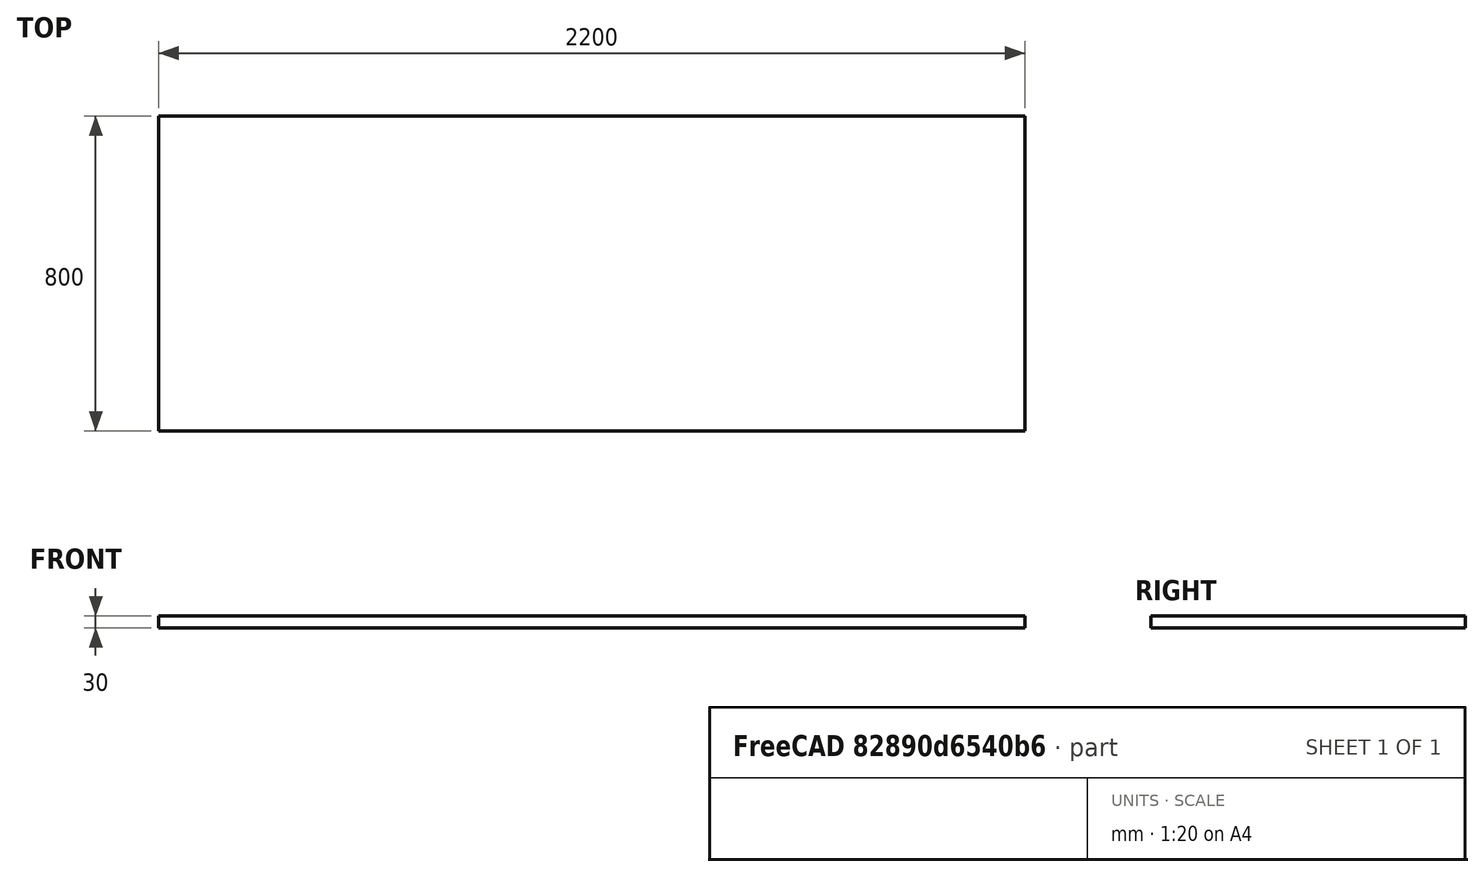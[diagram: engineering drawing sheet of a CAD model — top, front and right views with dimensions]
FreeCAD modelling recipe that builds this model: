
FCSTD DOCUMENT  (FreeCAD 1.0R39109 (Git))
Label: 021_top_sheet_30mm
License: All rights reserved
LicenseURL: http://en.wikipedia.org/wiki/All_rights_reserved
objects: Spreadsheet::Sheet×1, Sketcher::SketchObject×1, PartDesign::Pad×1, PartDesign::Body×1
note: 6 computed .brp shape members not serialized (recipe doc carries the construction recipe); baked Part::Feature solids carry a one-line shape summary decoded from their .brp

FEATURE [Spreadsheet::Sheet] Spreadsheet
  cells = A4='length; B4(length)=2200; A5='width; B5(width)=800; A6='height; B6(height)=30
FEATURE [Sketcher::SketchObject] Sketch
  ArcFitTolerance = 1e-06
  AttachmentSupport = -> [XY_Plane]
  FullyConstrained = true
  MakeInternals = false
  MapMode = 5
  expr: Constraints[11] = Spreadsheet.length
  expr: Constraints[12] = Spreadsheet.width
  sketch-geometry (5):
    g0: LineSegment StartX=-1100 StartY=400 StartZ=0 EndX=-1100 EndY=-400 EndZ=0
    g1: LineSegment StartX=-1100 StartY=-400 StartZ=0 EndX=1100 EndY=-400 EndZ=0
    g2: LineSegment StartX=1100 StartY=-400 StartZ=0 EndX=1100 EndY=400 EndZ=0
    g3: LineSegment StartX=1100 StartY=400 StartZ=0 EndX=-1100 EndY=400 EndZ=0
    g4: LineSegment [constr] StartX=-1100 StartY=400 StartZ=0 EndX=1100 EndY=-400 EndZ=0
  constraints (13):
    c: Coincident(g0,g1)
    c: Coincident(g1,g2)
    c: Coincident(g2,g3)
    c: Coincident(g3,g0)
    c: Vertical(g0)
    c: Vertical(g2)
    c: Horizontal(g1)
    c: Horizontal(g3)
    c: Coincident(g4,g0)
    c: Coincident(g4,g1)
    c: Symmetric(g4,g4,g-1)
    c: DistanceX(g3,g3) = 2200
    c: DistanceY(g0,g0) = 800
FEATURE [PartDesign::Pad] Pad
  Direction = (0,0,1)
  Length = 30
  Length2 = 10
  Midplane = true
  Profile = -> Sketch
  ReferenceAxis = -> Sketch [N_Axis]
  Suppressed = false
  Type = 0
  expr: Length = Spreadsheet.height
FEATURE [PartDesign::Body] Body
  AllowCompound = false
  Group = -> [Sketch,Pad]
  Origin = -> Origin
  Tip = -> Pad
